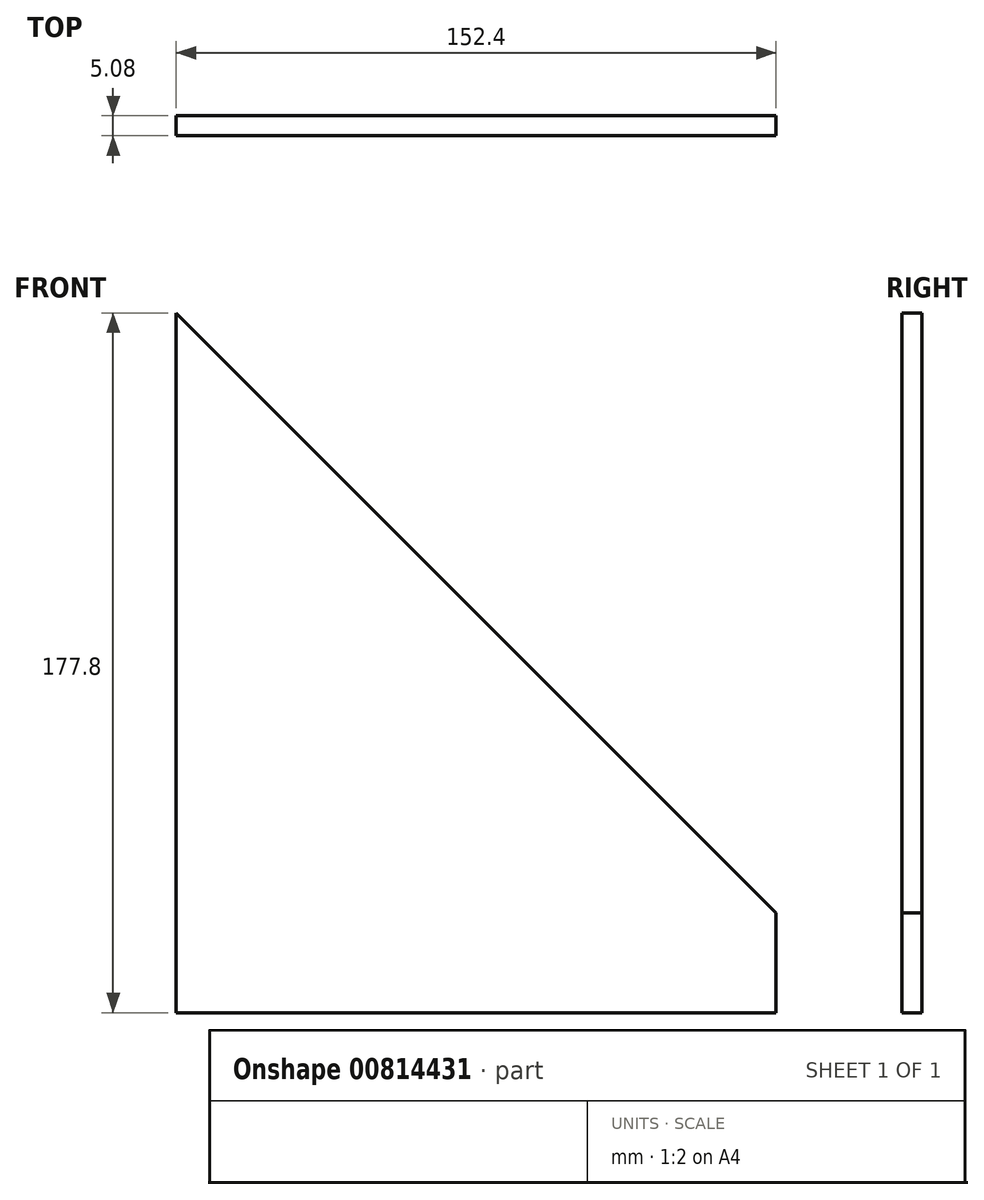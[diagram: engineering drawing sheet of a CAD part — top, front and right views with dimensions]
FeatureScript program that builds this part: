
annotation { "Feature Type Name" : "Feature", "Feature Type Description" : "" }
export const myFeature = defineFeature(function(context is Context, id is Id, definition is map)
    precondition{}
    {
        {
            var Q0;
            Q0=qCreatedBy(makeId("Front.planeOp"),FACE);
            var sketch = newSketch(context, id + "F0", { "sketchPlane" : qUnion([Q0])});
            skLineSegment(sketch, "E0.bottom", {"start": v(-169.92, 102.79) * mm, "end": v(-17.52, 102.79) * mm});
            skLineSegment(sketch, "E0.top", {"start": v(-169.92, -49.61) * mm, "end": v(-17.52, -49.61) * mm});
            skLineSegment(sketch, "E0.left", {"start": v(-169.92, 102.79) * mm, "end": v(-169.92, -49.61) * mm});
            skLineSegment(sketch, "E0.right", {"start": v(-17.52, 102.79) * mm, "end": v(-17.52, -49.61) * mm});
            skSolve(sketch);
        }
        {
            var Q0;
            Q0=makeQuery(id+"F0.imprint","IMPRINT",FACE,{"disambiguationData":[TD([[makeQuery(id+"F0.imprint","IMPRINT",EDGE,{"derivedFrom":sQuery(id+"F0.wireOp",EDGE,"E0.bottom")}),-1.0]])]});
            extrude(context, id + "F1", {"entities" : qUnion([Q0]), "depth" : 5.08 * mm, "offsetDistance" : 25.4 * mm});
        }
        {
            var Q0;
            Q0=makeQuery(id+"F1.opExtrude","CAP_FACE",FACE,{"disambiguationData":[OSD([sQuery(id+"F0.wireOp",EDGE,"E0.bottom"),sQuery(id+"F0.wireOp",EDGE,"E0.top"),sQuery(id+"F0.wireOp",EDGE,"E0.left"),sQuery(id+"F0.wireOp",EDGE,"E0.right")])],"isStart":false});
            var sketch = newSketch(context, id + "F2", { "sketchPlane" : qUnion([Q0])});
            skLineSegment(sketch, "E1", {"start": v(-169.92, 102.79) * mm, "end": v(-17.52, -49.61) * mm});
            skSolve(sketch);
        }
        {
            var Q0;
            Q0=makeQuery(id+"F2.imprint","IMPRINT",FACE,{"disambiguationData":[TD([[makeQuery(id+"F2.imprint","IMPRINT",EDGE,{"derivedFrom":sQuery(id+"F2.wireOp",EDGE,"E1")}),1.0]])]});
            extrude(context, id + "F3", {"entities" : qUnion([Q0]), "operationType" : NewBodyOperationType.REMOVE, "oppositeDirection" : true, "depth" : 5.08 * mm, "offsetDistance" : 25.4 * mm});
        }
        {
            var Q0;
            Q0=makeQuery(id+"F1.opExtrude","SWEPT_FACE",FACE,{"disambiguationData":[OSD([sQuery(id+"F0.wireOp",EDGE,"E0.top")])]});
            extrude(context, id + "F4", {"entities" : qUnion([Q0]), "operationType" : NewBodyOperationType.ADD, "depth" : 25.4 * mm, "offsetDistance" : 25.4 * mm});
        }
    });
